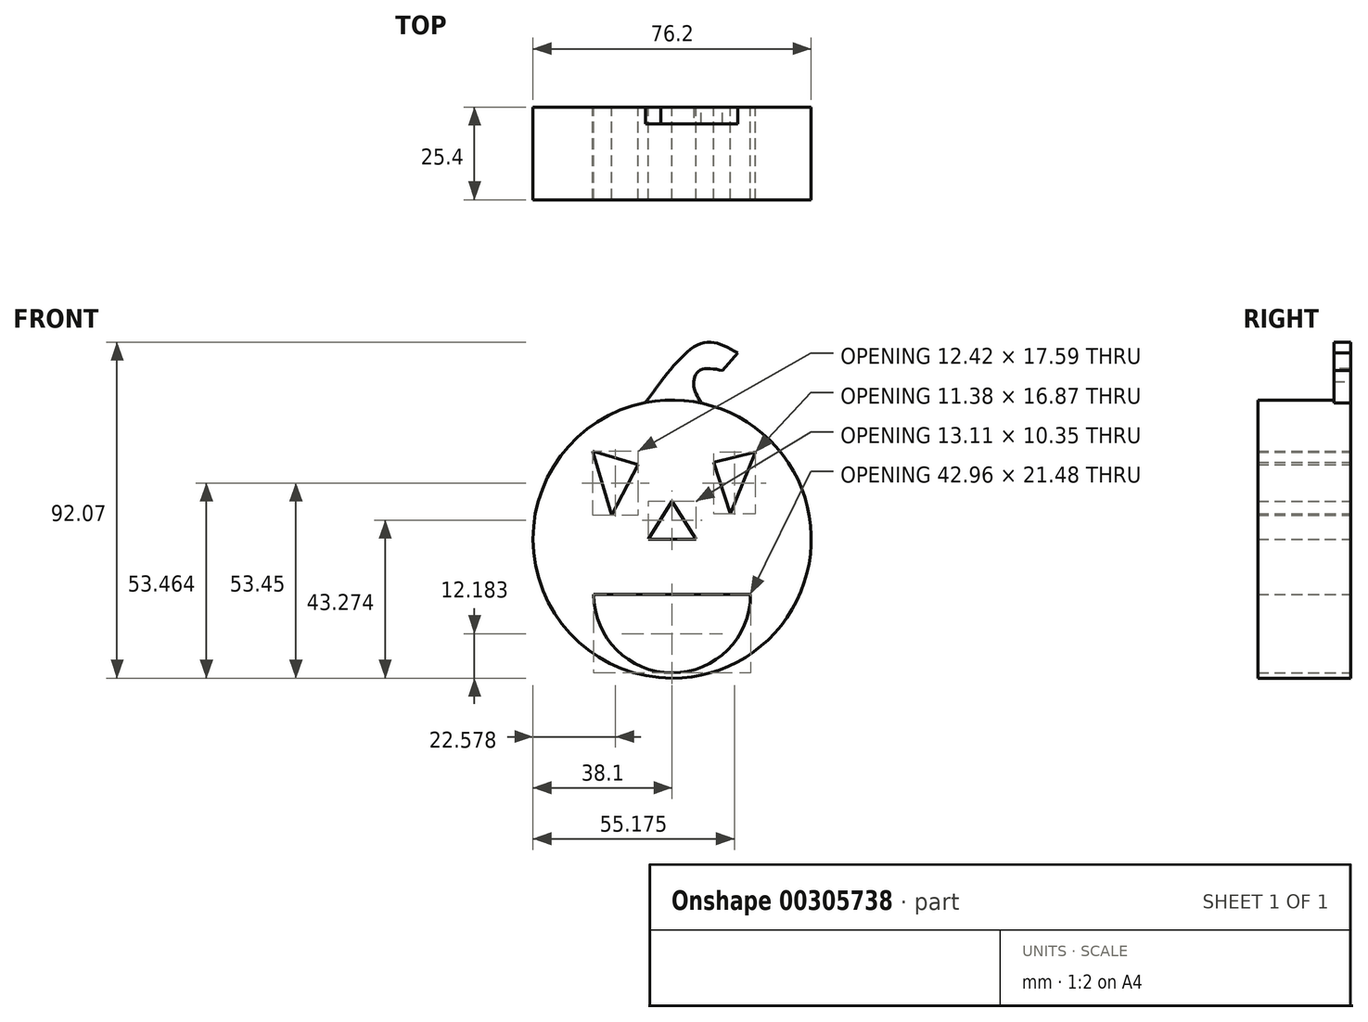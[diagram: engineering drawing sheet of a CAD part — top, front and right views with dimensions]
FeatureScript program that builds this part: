
annotation { "Feature Type Name" : "Feature", "Feature Type Description" : "" }
export const myFeature = defineFeature(function(context is Context, id is Id, definition is map)
    precondition{}
    {
        {
            var Q0;
            Q0=qCreatedBy(makeId("Front.planeOp"),FACE);
            var sketch = newSketch(context, id + "F0", { "sketchPlane" : qUnion([Q0])});
            skCircle(sketch, "E0", {"center": v(0, 0) * mm, "radius": 38.1 * mm});
            skLineSegment(sketch, "E1", {"start": v(11.38, 21.04) * mm, "end": v(15.99, 6.93) * mm});
            skLineSegment(sketch, "E2", {"start": v(15.99, 6.93) * mm, "end": v(22.77, 23.8) * mm});
            skLineSegment(sketch, "E3", {"start": v(-21.73, 24.15) * mm, "end": v(-16.56, 6.55) * mm});
            skLineSegment(sketch, "E4", {"start": v(-16.56, 6.55) * mm, "end": v(-9.31, 20.35) * mm});
            skLineSegment(sketch, "E5", {"start": v(-9.31, 20.35) * mm, "end": v(-21.73, 24.15) * mm});
            skLineSegment(sketch, "E6", {"start": v(-21.73, 24.15) * mm, "end": v(-9.31, 20.35) * mm});
            skLineSegment(sketch, "E7", {"start": v(11.38, 21.04) * mm, "end": v(22.77, 23.8) * mm});
            skLineSegment(sketch, "E8", {"start": v(0, 10.35) * mm, "end": v(-6.55, 0) * mm});
            skLineSegment(sketch, "E9", {"start": v(-6.55, 0) * mm, "end": v(6.55, 0) * mm});
            skLineSegment(sketch, "E10", {"start": v(6.55, 0) * mm, "end": v(0, 10.35) * mm});
            skFitSpline(sketch, "E11", {"points": [v(-3.1, 43.12) * mm, v(8.62, 53.81) * mm, v(17.94, 51.05) * mm], "startDerivative": vector(20.81, 26.17) * mm, "endDerivative": vector(21.29, -11.85) * mm});
            skLineSegment(sketch, "E12", {"start": v(17.94, 51.05) * mm, "end": v(13.8, 46.22) * mm});
            skFitSpline(sketch, "E13", {"points": [v(13.8, 46.22) * mm, v(7.59, 46.22) * mm, v(5.86, 42.43) * mm, v(7.97, 37.26) * mm], "startDerivative": vector(-19.7, 3.56) * mm, "endDerivative": vector(8.78, -15) * mm});
            skFitSpline(sketch, "E14", {"points": [v(-3.1, 43.12) * mm, v(-7.33, 37.39) * mm], "startDerivative": vector(-4.23, -5.7) * mm, "endDerivative": vector(-4.23, -5.7) * mm});
            skArc(sketch, "E15", {"start": v(-21.48, -15.18) * mm, "mid": v(0, -36.66) * mm, "end": v(21.48, -15.18) * mm});
            skLineSegment(sketch, "E16.trimOffspring", {"start": v(-21.48, -15.18) * mm, "end": v(21.48, -15.18) * mm});
            skPoint(sketch, "E17.start.orphan", {"position": v(-92.1, 0) * mm});
            skSolve(sketch);
        }
        {
            var Q0;
            Q0=makeQuery(id+"F0.imprint","IMPRINT",FACE,{"disambiguationData":[TD([[makeQuery(id+"F0.imprint","IMPRINT",EDGE,{"derivedFrom":sQuery(id+"F0.wireOp",EDGE,"E1")}),-1.0]])]});
            extrude(context, id + "F1", {"entities" : qUnion([Q0]), "depth" : 25.4 * mm});
        }
        {
            var Q0;
            Q0=makeQuery(id+"F0.imprint","IMPRINT",FACE,{"disambiguationData":[TD([[makeQuery(id+"F0.imprint","IMPRINT",EDGE,{"derivedFrom":sQuery(id+"F0.wireOp",EDGE,"E11")}),-1.0]])]});
            extrude(context, id + "F2", {"entities" : qUnion([Q0]), "operationType" : NewBodyOperationType.ADD, "depth" : 4.57 * mm});
        }
    });
